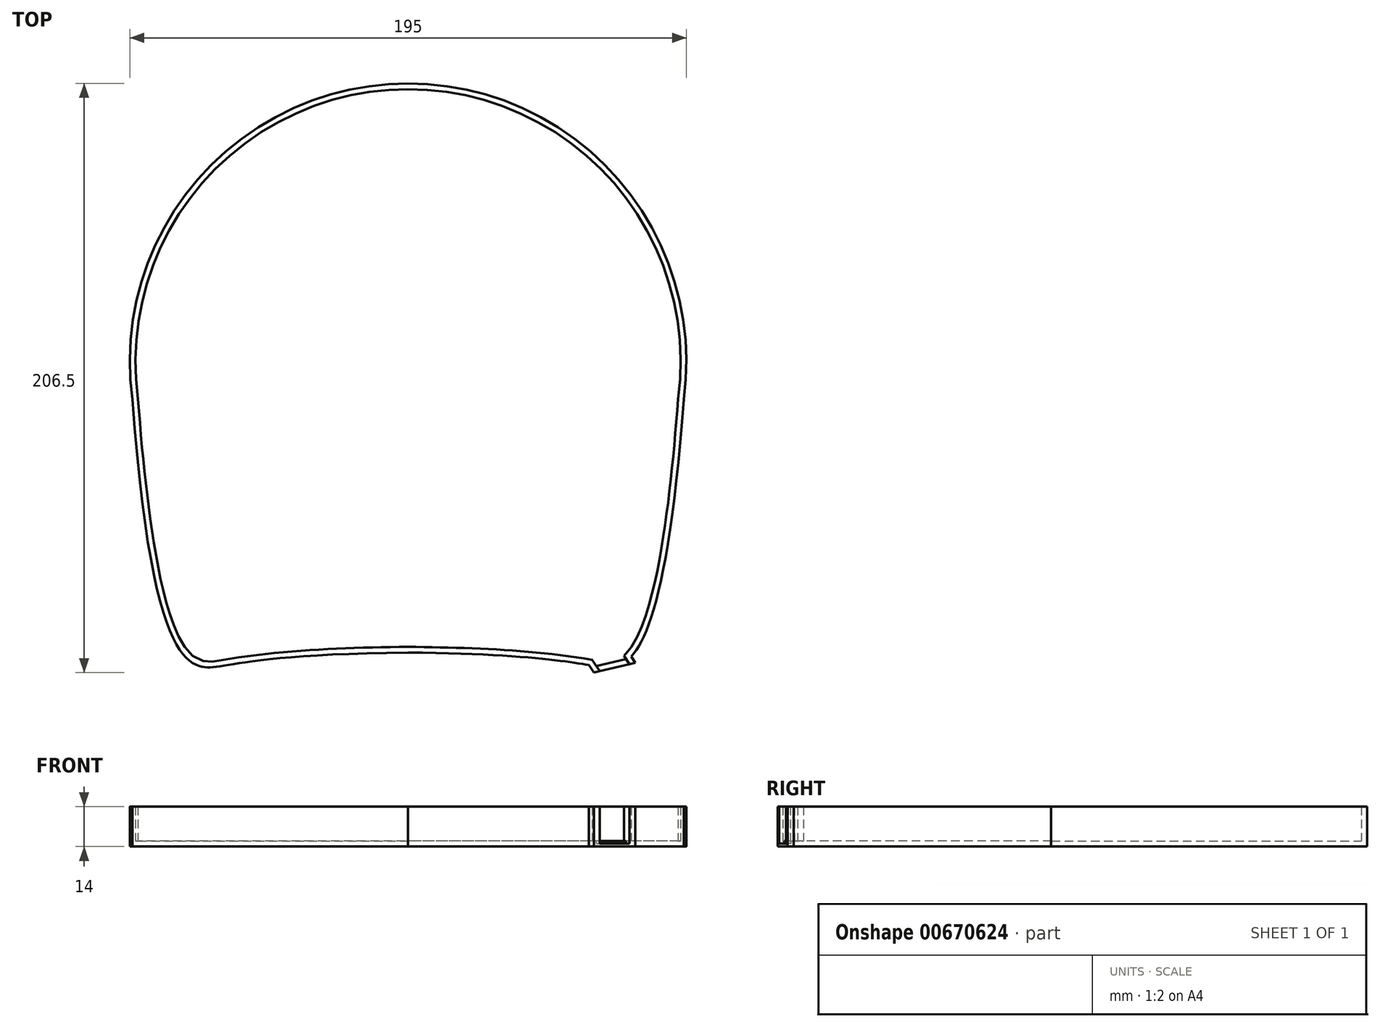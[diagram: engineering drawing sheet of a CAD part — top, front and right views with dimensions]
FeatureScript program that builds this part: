
annotation { "Feature Type Name" : "Feature", "Feature Type Description" : "" }
export const myFeature = defineFeature(function(context is Context, id is Id, definition is map)
    precondition{}
    {
        {
            var Q0;
            Q0=qCreatedBy(makeId("Top.planeOp"),FACE);
            var sketch = newSketch(context, id + "F0", { "sketchPlane" : qUnion([Q0])});
            skCircle(sketch, "E0", {"center": v(0, 0) * mm, "radius": 97.5 * mm});
            skLineSegment(sketch, "E1", {"start": v(0, 0) * mm, "end": v(-72.14, -106.95) * mm});
            skLineSegment(sketch, "E2", {"start": v(0, 0) * mm, "end": v(0, -102) * mm});
            skPoint(sketch, "E3", {"position": v(-97.5, 0) * mm});
            skFitSpline(sketch, "E4", {"points": [v(-97.5, 0) * mm, v(-72.14, -106.95) * mm, v(0, -102) * mm], "startDerivative": vector(31.45, -501.43) * mm, "endDerivative": vector(399.28, 3.6) * mm});
            skFitSpline(sketch, "E5.MirrorCS", {"points": [v(97.5, 0) * mm, v(72.14, -106.95) * mm, v(0, -102) * mm], "startDerivative": vector(-31.45, -501.43) * mm, "endDerivative": vector(-399.28, 3.6) * mm});
            skLineSegment(sketch, "E6.MirrorCS", {"start": v(0, 0) * mm, "end": v(72.14, -106.95) * mm});
            skLineSegment(sketch, "E7", {"start": v(72.14, -106.95) * mm, "end": v(73.81, -109.43) * mm});
            skLineSegment(sketch, "E8", {"start": v(73.81, -109.43) * mm, "end": v(68.01, -113.35) * mm});
            skLineSegment(sketch, "E9", {"start": v(68.01, -113.35) * mm, "end": v(63.31, -106.38) * mm});
            skLineSegment(sketch, "E10.MirrorCS", {"start": v(73.81, -109.43) * mm, "end": v(79.62, -105.52) * mm});
            skLineSegment(sketch, "E11", {"start": v(79.62, -105.52) * mm, "end": v(78.16, -103.36) * mm});
            skLineSegment(sketch, "E12", {"start": v(79.62, -105.52) * mm, "end": v(65.08, -109) * mm});
            skSolve(sketch);
        }
        {
            var Q0;
            {var subQ0=sQuery(id+"F0.wireOp",EDGE,"E4");var subQ1=sQuery(id+"F0.wireOp",EDGE,"E0");var subQ2=makeQuery(id+"F0.imprint","INTERSECT",VERTEX,{"disambiguationData":[OD(0.0)],"derivedFrom":[subQ1,subQ0]});Q0=makeQuery(id+"F0.imprint","IMPRINT",FACE,{"disambiguationData":[TD([[makeQuery(id+"F0.imprint","IMPRINT",EDGE,{"disambiguationData":[TD([[subQ2,-1.0]])],"derivedFrom":subQ1}),1.0]])]});}
            var Q1;
            {var subQ0=sQuery(id+"F0.wireOp",EDGE,"E5.MirrorCS");var subQ1=sQuery(id+"F0.wireOp",EDGE,"E0");var subQ2=makeQuery(id+"F0.imprint","INTERSECT",VERTEX,{"disambiguationData":[OD(0.0)],"derivedFrom":[subQ1,subQ0]});Q1=makeQuery(id+"F0.imprint","IMPRINT",FACE,{"disambiguationData":[TD([[makeQuery(id+"F0.imprint","IMPRINT",EDGE,{"disambiguationData":[TD([[subQ2,1.0]])],"derivedFrom":subQ1}),1.0]])]});}
            var Q2;
            {var subQ0=sQuery(id+"F0.wireOp",EDGE,"E4");var subQ1=sQuery(id+"F0.wireOp",EDGE,"E0");var subQ2=makeQuery(id+"F0.imprint","INTERSECT",VERTEX,{"disambiguationData":[OD(1.0)],"derivedFrom":[subQ1,subQ0]});Q2=makeQuery(id+"F0.imprint","IMPRINT",FACE,{"disambiguationData":[TD([[makeQuery(id+"F0.imprint","IMPRINT",EDGE,{"disambiguationData":[TD([[subQ2,-1.0]])],"derivedFrom":subQ1}),-1.0]])]});}
            var Q3;
            {var subQ0=sQuery(id+"F0.wireOp",EDGE,"E1");var subQ1=sQuery(id+"F0.wireOp",EDGE,"E0");var subQ2=makeQuery(id+"F0.imprint","INTERSECT",VERTEX,{"derivedFrom":[subQ1,subQ0]});Q3=makeQuery(id+"F0.imprint","IMPRINT",FACE,{"disambiguationData":[TD([[makeQuery(id+"F0.imprint","IMPRINT",EDGE,{"disambiguationData":[TD([[subQ2,-1.0]])],"derivedFrom":subQ1}),-1.0]])]});}
            var Q4;
            {var subQ0=sQuery(id+"F0.wireOp",EDGE,"E5.MirrorCS");var subQ1=sQuery(id+"F0.wireOp",EDGE,"E0");var subQ2=makeQuery(id+"F0.imprint","INTERSECT",VERTEX,{"disambiguationData":[OD(1.0)],"derivedFrom":[subQ1,subQ0]});Q4=makeQuery(id+"F0.imprint","IMPRINT",FACE,{"disambiguationData":[TD([[makeQuery(id+"F0.imprint","IMPRINT",EDGE,{"disambiguationData":[TD([[subQ2,1.0]])],"derivedFrom":subQ1}),-1.0]])]});}
            var Q5;
            {var subQ3=sQuery(id+"F0.wireOp",EDGE,"E11");Q5=makeQuery(id+"F0.imprint","IMPRINT",FACE,{"disambiguationData":[TD([[makeQuery(id+"F0.imprint","IMPRINT",EDGE,{"derivedFrom":subQ3}),1.0]])]});}
            var Q6;
            {var subQ1=sQuery(id+"F0.wireOp",EDGE,"E5.MirrorCS");var subQ3=sQuery(id+"F0.wireOp",EDGE,"E9");var subQ4=makeQuery(id+"F0.imprint","INTERSECT",VERTEX,{"derivedFrom":[subQ1,subQ3]});Q6=makeQuery(id+"F0.imprint","IMPRINT",FACE,{"disambiguationData":[TD([[makeQuery(id+"F0.imprint","IMPRINT",EDGE,{"disambiguationData":[TD([[subQ4,1.0]])],"derivedFrom":subQ3}),-1.0]])]});}
            var Q7;
            {var subQ1=sQuery(id+"F0.wireOp",EDGE,"E2");var subQ6=sQuery(id+"F0.wireOp",EDGE,"E0");var subQ7=makeQuery(id+"F0.imprint","INTERSECT",VERTEX,{"derivedFrom":[subQ6,subQ1]});Q7=makeQuery(id+"F0.imprint","IMPRINT",FACE,{"disambiguationData":[TD([[makeQuery(id+"F0.imprint","IMPRINT",EDGE,{"disambiguationData":[TD([[subQ7,-1.0]])],"derivedFrom":subQ6}),-1.0]])]});}
            var Q8;
            {var subQ3=sQuery(id+"F0.wireOp",EDGE,"E0");var subQ5=sQuery(id+"F0.wireOp",EDGE,"E4");var subQ10=makeQuery(id+"F0.imprint","INTERSECT",VERTEX,{"disambiguationData":[OD(0.0)],"derivedFrom":[subQ3,subQ5]});Q8=makeQuery(id+"F0.imprint","IMPRINT",FACE,{"disambiguationData":[TD([[makeQuery(id+"F0.imprint","IMPRINT",EDGE,{"disambiguationData":[TD([[subQ10,1.0]])],"derivedFrom":subQ3}),1.0]])]});}
            var Q9;
            {var subQ0=sQuery(id+"F0.wireOp",EDGE,"E1");var subQ1=sQuery(id+"F0.wireOp",EDGE,"E0");var subQ2=makeQuery(id+"F0.imprint","INTERSECT",VERTEX,{"derivedFrom":[subQ1,subQ0]});Q9=makeQuery(id+"F0.imprint","IMPRINT",FACE,{"disambiguationData":[TD([[makeQuery(id+"F0.imprint","IMPRINT",EDGE,{"disambiguationData":[TD([[subQ2,-1.0]])],"derivedFrom":subQ1}),1.0]])]});}
            var Q10;
            {var subQ0=sQuery(id+"F0.wireOp",EDGE,"E2");var subQ1=sQuery(id+"F0.wireOp",EDGE,"E0");var subQ2=makeQuery(id+"F0.imprint","INTERSECT",VERTEX,{"derivedFrom":[subQ1,subQ0]});Q10=makeQuery(id+"F0.imprint","IMPRINT",FACE,{"disambiguationData":[TD([[makeQuery(id+"F0.imprint","IMPRINT",EDGE,{"disambiguationData":[TD([[subQ2,-1.0]])],"derivedFrom":subQ1}),1.0]])]});}
            extrude(context, id + "F1", {"entities" : qUnion([Q0, Q1, Q2, Q3, Q4, Q5, Q6, Q7, Q8, Q9, Q10]), "depth" : 14 * mm, "offsetDistance" : 25 * mm});
        }
        {
            var Q0;
            Q0=makeQuery(id+"F1.opExtrude","CAP_FACE",FACE,{"disambiguationData":[OSD([sQuery(id+"F0.wireOp",EDGE,"E0"),sQuery(id+"F0.wireOp",EDGE,"E4"),sQuery(id+"F0.wireOp",EDGE,"E5.MirrorCS")])],"isStart":false});
            shell(context, id + "F2", {"entities" : qUnion([Q0]), "thickness" : 2 * mm});
        }
        {
            var Q0;
            Q0=makeQuery(id+"F1.opExtrude","CAP_FACE",FACE,{"disambiguationData":[OSD([sQuery(id+"F0.wireOp",EDGE,"E0"),sQuery(id+"F0.wireOp",EDGE,"E4"),sQuery(id+"F0.wireOp",EDGE,"E5.MirrorCS"),sQuery(id+"F0.wireOp",EDGE,"E8"),sQuery(id+"F0.wireOp",EDGE,"E9"),sQuery(id+"F0.wireOp",EDGE,"E10.MirrorCS"),sQuery(id+"F0.wireOp",EDGE,"E11")])],"isStart":false});
            var sketch = newSketch(context, id + "F3", { "sketchPlane" : qUnion([Q0])});
            skLineSegment(sketch, "E13", {"start": v(65.96, -106.73) * mm, "end": v(76.35, -104.25) * mm});
            skLineSegment(sketch, "E14", {"start": v(76.35, -104.25) * mm, "end": v(77.54, -106.02) * mm});
            skLineSegment(sketch, "E15", {"start": v(65.96, -106.73) * mm, "end": v(67.16, -108.5) * mm});
            skLineSegment(sketch, "E16", {"start": v(67.16, -108.5) * mm, "end": v(77.54, -106.02) * mm});
            skSolve(sketch);
        }
        {
            var Q0;
            Q0=makeQuery(id+"F3.imprint","IMPRINT",FACE,{"disambiguationData":[TD([[makeQuery(id+"F3.imprint","IMPRINT",EDGE,{"derivedFrom":sQuery(id+"F3.wireOp",EDGE,"E13")}),1.0]])]});
            extrude(context, id + "F4", {"entities" : qUnion([Q0]), "operationType" : NewBodyOperationType.REMOVE, "oppositeDirection" : true, "depth" : 13 * mm, "offsetDistance" : 25 * mm});
        }
    });
